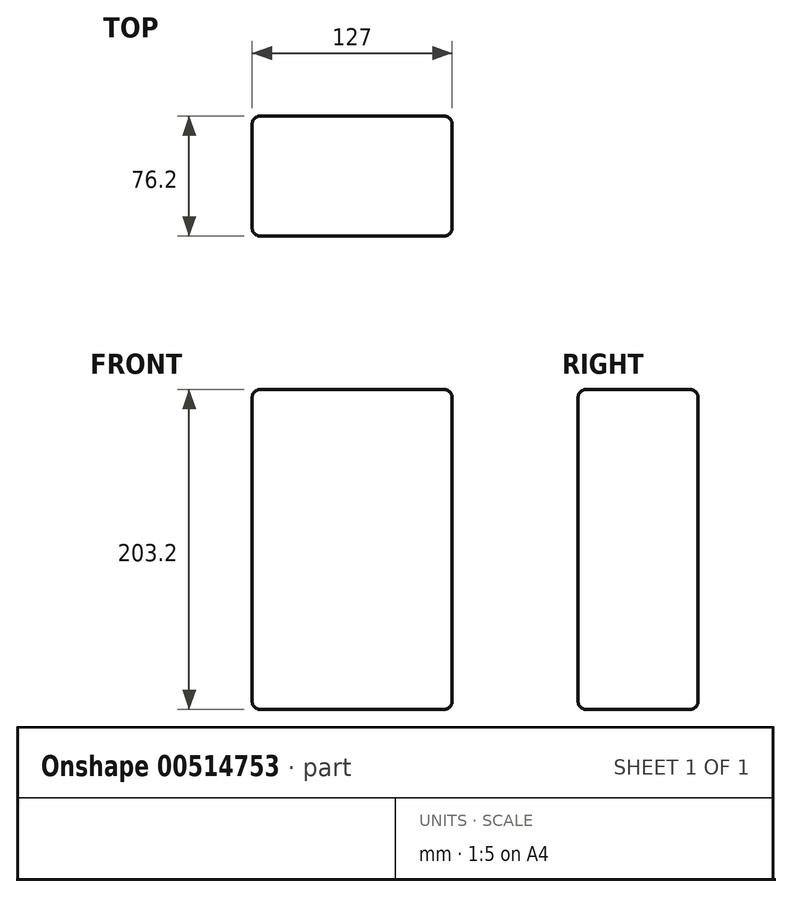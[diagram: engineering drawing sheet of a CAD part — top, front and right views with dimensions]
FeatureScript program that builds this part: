
annotation { "Feature Type Name" : "Feature", "Feature Type Description" : "" }
export const myFeature = defineFeature(function(context is Context, id is Id, definition is map)
    precondition{}
    {
        {
            var Q0;
            Q0=qCreatedBy(makeId("Right.planeOp"),FACE);
            var sketch = newSketch(context, id + "F0", { "sketchPlane" : qUnion([Q0])});
            skLineSegment(sketch, "E0.bottom", {"start": v(-29.02, 139.92) * mm, "end": v(47.18, 139.92) * mm});
            skLineSegment(sketch, "E0.top", {"start": v(-29.02, -63.28) * mm, "end": v(47.18, -63.28) * mm});
            skLineSegment(sketch, "E0.left", {"start": v(-29.02, 139.92) * mm, "end": v(-29.02, -63.28) * mm});
            skLineSegment(sketch, "E0.right", {"start": v(47.18, 139.92) * mm, "end": v(47.18, -63.28) * mm});
            skSolve(sketch);
        }
        {
            var Q0;
            Q0 = qSketchRegion(id + "F0", true);
            extrude(context, id + "F1", {"entities" : qUnion([Q0]), "depth" : 127 * mm, "offsetDistance" : 25.4 * mm});
        }
        {
            var Q0;
            Q0=makeQuery(id+"F1.opExtrude","SWEPT_FACE",FACE,{"disambiguationData":[OSD([sQuery(id+"F0.wireOp",EDGE,"E0.left")])]});
            var Q1;
            Q1=makeQuery(id+"F1.opExtrude","CAP_FACE",FACE,{"disambiguationData":[OSD([sQuery(id+"F0.wireOp",EDGE,"E0.bottom"),sQuery(id+"F0.wireOp",EDGE,"E0.top"),sQuery(id+"F0.wireOp",EDGE,"E0.left"),sQuery(id+"F0.wireOp",EDGE,"E0.right")])],"isStart":false});
            var Q2;
            Q2=makeQuery(id+"F1.opExtrude","SWEPT_FACE",FACE,{"disambiguationData":[OSD([sQuery(id+"F0.wireOp",EDGE,"E0.bottom")])]});
            var Q3;
            Q3=makeQuery(id+"F1.opExtrude","CAP_FACE",FACE,{"disambiguationData":[OSD([sQuery(id+"F0.wireOp",EDGE,"E0.bottom"),sQuery(id+"F0.wireOp",EDGE,"E0.top"),sQuery(id+"F0.wireOp",EDGE,"E0.left"),sQuery(id+"F0.wireOp",EDGE,"E0.right")])],"isStart":true});
            var Q4;
            Q4=makeQuery(id+"F1.opExtrude","CAP_EDGE",EDGE,{"disambiguationData":[OSD([sQuery(id+"F0.wireOp",EDGE,"E0.top")])],"isStart":false});
            var Q5;
            Q5=makeQuery(id+"F1.opExtrude","SWEPT_FACE",FACE,{"disambiguationData":[OSD([sQuery(id+"F0.wireOp",EDGE,"E0.right")])]});
            fillet(context, id + "F2", {"entities" : qUnion([Q0, Q1, Q2, Q3, Q4, Q5]), "radius" : 5.08 * mm, "tangentPropagation" : true, "allowEdgeOverflow" : false});
        }
    });
